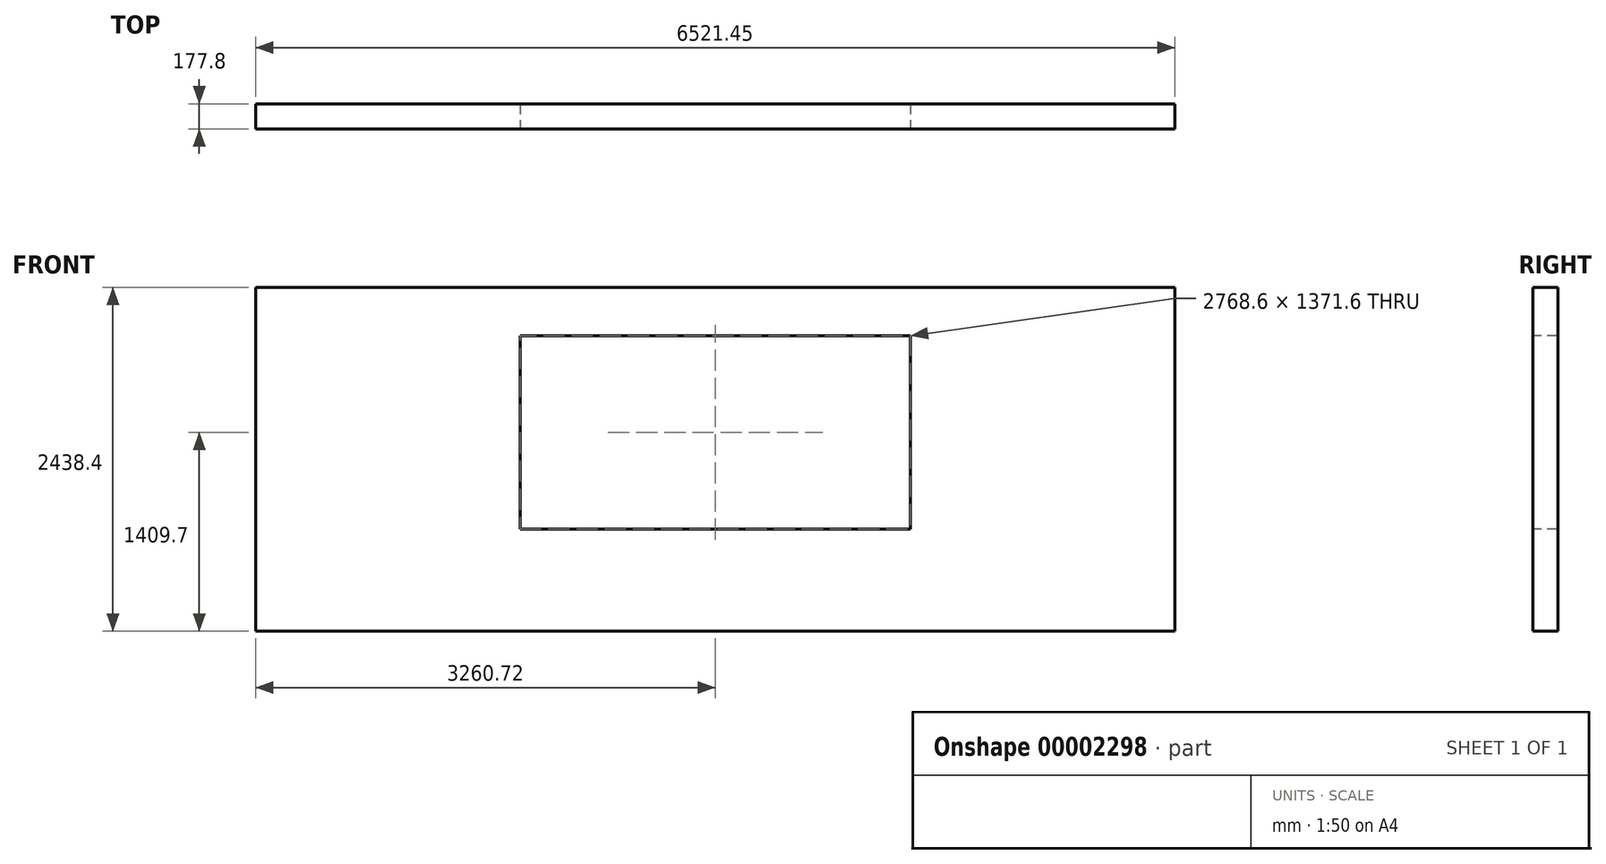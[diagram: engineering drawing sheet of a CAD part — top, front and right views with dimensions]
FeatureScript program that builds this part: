
annotation { "Feature Type Name" : "Feature", "Feature Type Description" : "" }
export const myFeature = defineFeature(function(context is Context, id is Id, definition is map)
    precondition{}
    {
        {
            var Q0;
            Q0=qCreatedBy(makeId("Front.planeOp"),FACE);
            var sketch = newSketch(context, id + "F0", { "sketchPlane" : qUnion([Q0])});
            skLineSegment(sketch, "E0.bottom", {"start": v(0, 0) * mm, "end": v(6521.45, 0) * mm});
            skLineSegment(sketch, "E0.top", {"start": v(0, 2438.4) * mm, "end": v(6521.45, 2438.4) * mm});
            skLineSegment(sketch, "E0.left", {"start": v(0, 0) * mm, "end": v(0, 2438.4) * mm});
            skLineSegment(sketch, "E0.right", {"start": v(6521.45, 0) * mm, "end": v(6521.45, 2438.4) * mm});
            skSolve(sketch);
        }
        {
            var Q0;
            Q0 = qSketchRegion(id + "F0", true);
            extrude(context, id + "F1", {"entities" : qUnion([Q0]), "depth" : 177.8 * mm});
        }
        {
            var Q0;
            Q0=makeQuery(id+"F1.opExtrude","CAP_FACE",FACE,{"disambiguationData":[OSD([sQuery(id+"F0.wireOp",EDGE,"E0.bottom"),sQuery(id+"F0.wireOp",EDGE,"E0.top"),sQuery(id+"F0.wireOp",EDGE,"E0.left"),sQuery(id+"F0.wireOp",EDGE,"E0.right")])],"isStart":false});
            var sketch = newSketch(context, id + "F2", { "sketchPlane" : qUnion([Q0])});
            skLineSegment(sketch, "E1.bottom", {"start": v(1876.43, 723.9) * mm, "end": v(4645.03, 723.9) * mm});
            skLineSegment(sketch, "E1.top", {"start": v(1876.43, 2095.5) * mm, "end": v(4645.03, 2095.5) * mm});
            skLineSegment(sketch, "E1.left", {"start": v(1876.43, 723.9) * mm, "end": v(1876.43, 2095.5) * mm});
            skLineSegment(sketch, "E1.right", {"start": v(4645.03, 723.9) * mm, "end": v(4645.03, 2095.5) * mm});
            skSolve(sketch);
        }
        {
            var Q0;
            Q0=makeQuery(id+"F2.imprint","IMPRINT",FACE,{"disambiguationData":[TD([[makeQuery(id+"F2.imprint","IMPRINT",EDGE,{"derivedFrom":sQuery(id+"F2.wireOp",EDGE,"E1.bottom")}),1.0]])]});
            extrude(context, id + "F3", {"entities" : qUnion([Q0]), "operationType" : NewBodyOperationType.REMOVE, "oppositeDirection" : true, "depth" : 177.8 * mm});
        }
    });
